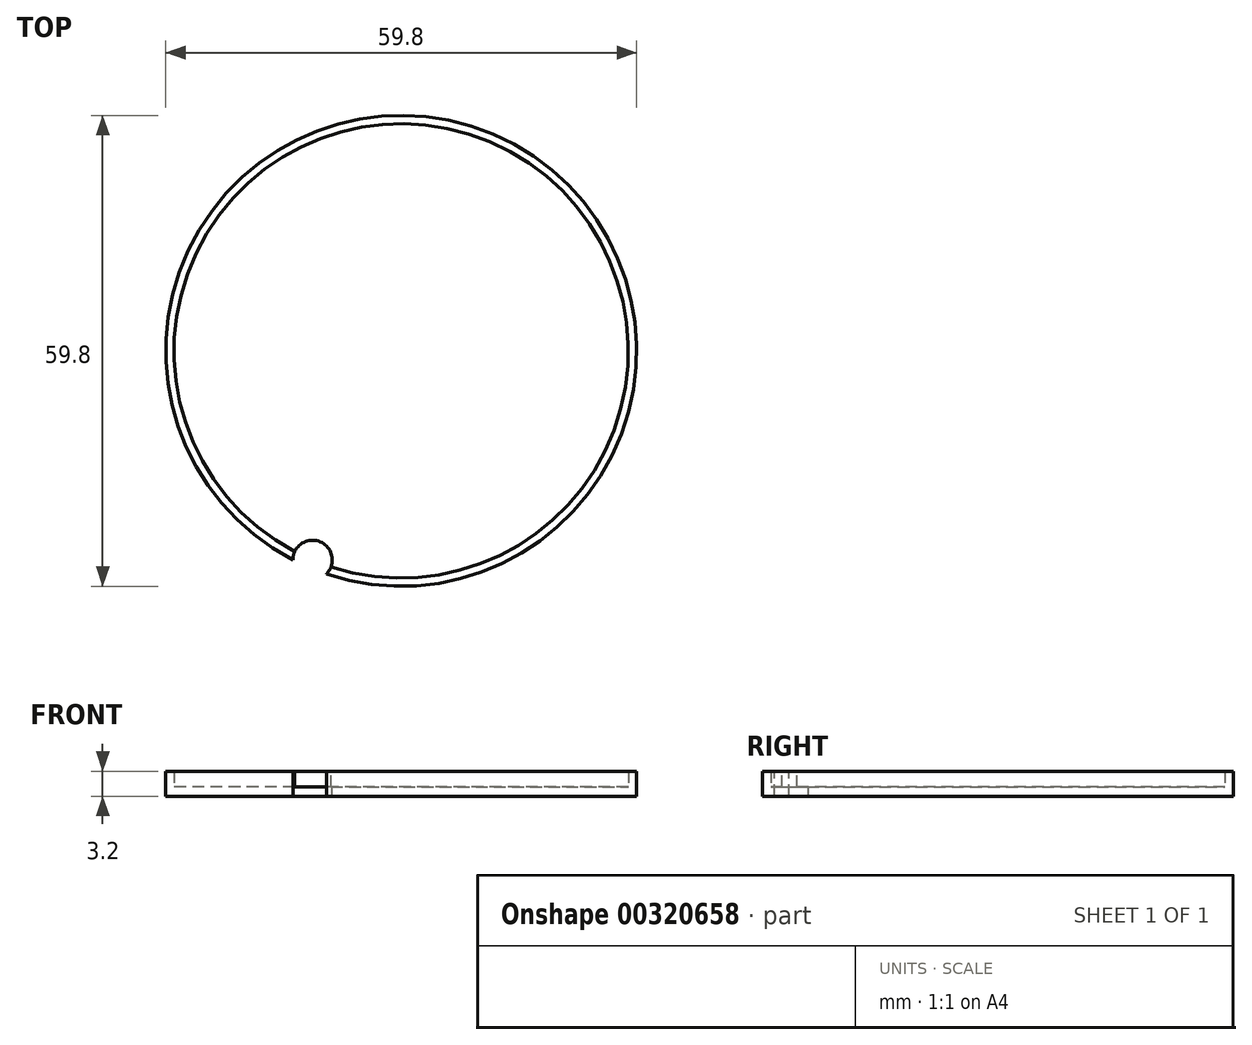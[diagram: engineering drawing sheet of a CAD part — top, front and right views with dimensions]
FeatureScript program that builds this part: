
annotation { "Feature Type Name" : "Feature", "Feature Type Description" : "" }
export const myFeature = defineFeature(function(context is Context, id is Id, definition is map)
    precondition{}
    {
        {
            var Q0;
            Q0=qCreatedBy(makeId("Top.planeOp"),FACE);
            var sketch = newSketch(context, id + "F0", { "sketchPlane" : qUnion([Q0])});
            skCircle(sketch, "E0", {"center": v(0, 0) * mm, "radius": 29.9 * mm});
            skSolve(sketch);
        }
        {
            var Q0;
            Q0 = qSketchRegion(id + "F0", true);
            extrude(context, id + "F1", {"entities" : qUnion([Q0]), "depth" : 1.2 * mm});
        }
        {
            var Q0;
            Q0=makeQuery(id+"F1.opExtrude","CAP_FACE",FACE,{"disambiguationData":[OSD([sQuery(id+"F0.wireOp",EDGE,"E0")])],"isStart":false});
            var sketch = newSketch(context, id + "F2", { "sketchPlane" : qUnion([Q0])});
            skCircle(sketch, "E1", {"center": v(0, 0) * mm, "radius": 29.9 * mm});
            skCircle(sketch, "E2", {"center": v(0, 0) * mm, "radius": 28.85 * mm});
            skSolve(sketch);
        }
        {
            var Q0;
            Q0 = qSketchRegion(id + "F2", true);
            extrude(context, id + "F3", {"entities" : qUnion([Q0]), "operationType" : NewBodyOperationType.ADD, "depth" : 2 * mm});
        }
        {
            var Q0;
            Q0=makeQuery(id+"F3.opExtrude","CAP_FACE",FACE,{"disambiguationData":[OSD([sQuery(id+"F2.wireOp",EDGE,"E1"),sQuery(id+"F2.wireOp",EDGE,"E2")])],"isStart":false});
            var sketch = newSketch(context, id + "F4", { "sketchPlane" : qUnion([Q0])});
            skCircle(sketch, "E3", {"center": v(-11.25, -26.57) * mm, "radius": 2.5 * mm});
            skSolve(sketch);
        }
        {
            var Q0;
            Q0 = qSketchRegion(id + "F4", true);
            extrude(context, id + "F5", {"entities" : qUnion([Q0]), "operationType" : NewBodyOperationType.REMOVE, "oppositeDirection" : true, "depth" : 3.2 * mm});
        }
    });
